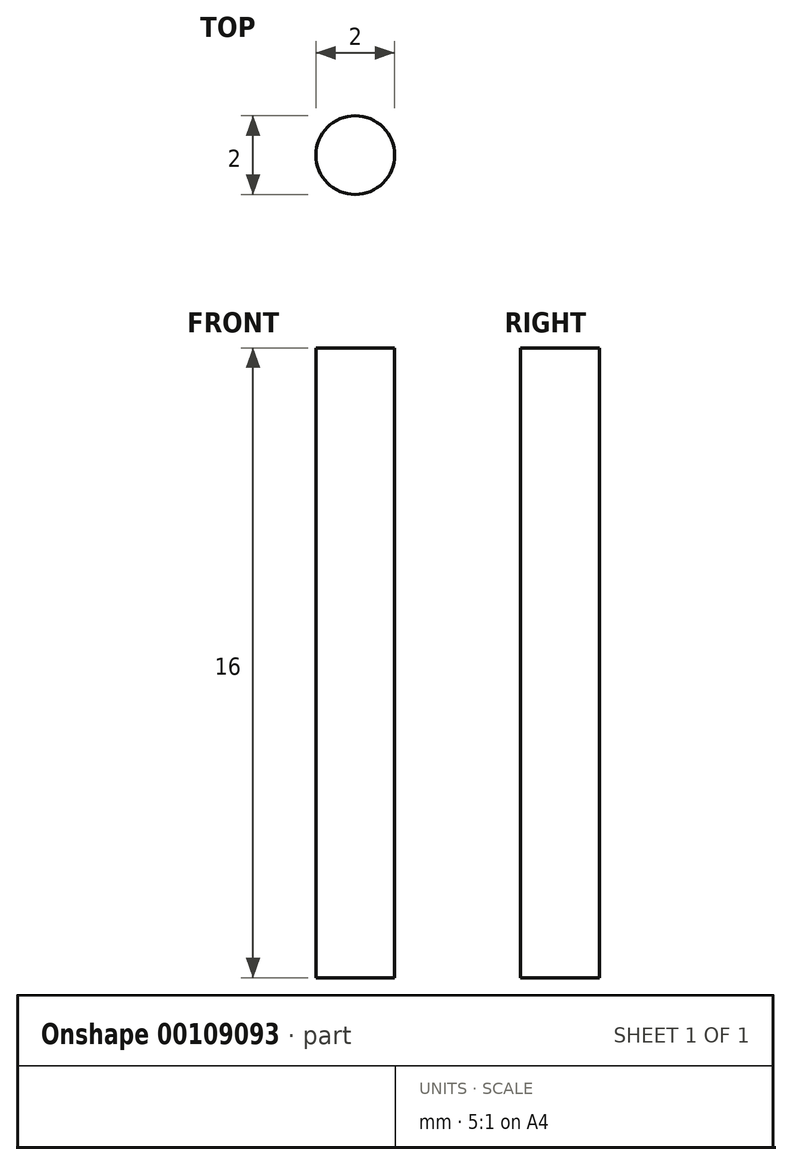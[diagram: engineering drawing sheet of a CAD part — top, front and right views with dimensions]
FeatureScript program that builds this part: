
annotation { "Feature Type Name" : "Feature", "Feature Type Description" : "" }
export const myFeature = defineFeature(function(context is Context, id is Id, definition is map)
    precondition{}
    {
        {
            var Q0;
            Q0=qCreatedBy(makeId("Top.planeOp"),FACE);
            var sketch = newSketch(context, id + "F0", { "sketchPlane" : qUnion([Q0])});
            skCircle(sketch, "E0", {"center": v(0, 0) * mm, "radius": 1 * mm});
            skSolve(sketch);
        }
        {
            var Q0;
            Q0=makeQuery(id+"F0.imprint","IMPRINT",FACE,{"disambiguationData":[TD([[makeQuery(id+"F0.imprint","IMPRINT",EDGE,{"derivedFrom":sQuery(id+"F0.wireOp",EDGE,"E0")}),1.0]])]});
            extrude(context, id + "F1", {"entities" : qUnion([Q0]), "depth" : 16 * mm});
        }
    });
